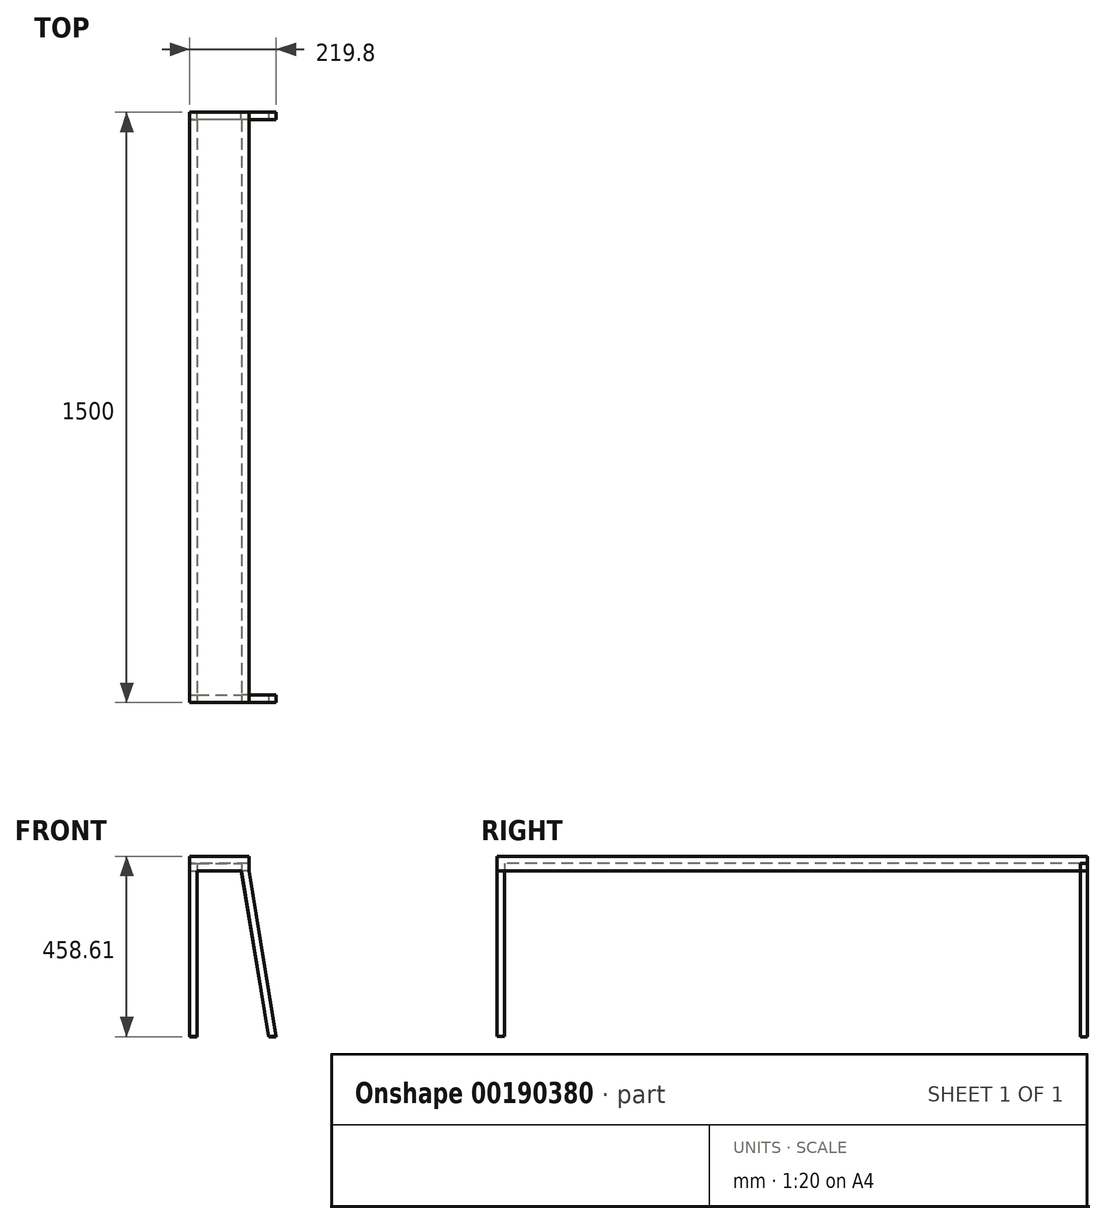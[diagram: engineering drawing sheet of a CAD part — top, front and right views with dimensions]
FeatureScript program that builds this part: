
annotation { "Feature Type Name" : "Feature", "Feature Type Description" : "" }
export const myFeature = defineFeature(function(context is Context, id is Id, definition is map)
    precondition{}
    {
        {
            var Q0;
            Q0=qCreatedBy(makeId("Front.planeOp"),FACE);
            var sketch = newSketch(context, id + "F0", { "sketchPlane" : qUnion([Q0])});
            skLineSegment(sketch, "E0.bottom", {"start": v(-19, 322.25) * mm, "end": v(131, 322.25) * mm});
            skLineSegment(sketch, "E0.top", {"start": v(-19, 303.25) * mm, "end": v(131, 303.25) * mm});
            skLineSegment(sketch, "E0.left", {"start": v(-19, 322.25) * mm, "end": v(-19, 303.25) * mm});
            skLineSegment(sketch, "E0.right", {"start": v(131, 322.25) * mm, "end": v(131, 303.25) * mm});
            skLineSegment(sketch, "E1", {"start": v(-19, 303.25) * mm, "end": v(-19, -116.75) * mm});
            skLineSegment(sketch, "E2", {"start": v(-19, -116.75) * mm, "end": v(0, -116.75) * mm});
            skLineSegment(sketch, "E3", {"start": v(0, -116.75) * mm, "end": v(0, 303.25) * mm});
            skLineSegment(sketch, "E4", {"start": v(131, 303.25) * mm, "end": v(200.52, -116.75) * mm});
            skLineSegment(sketch, "E5", {"start": v(200.52, -116.75) * mm, "end": v(181.52, -116.75) * mm});
            skLineSegment(sketch, "E6", {"start": v(181.52, -116.75) * mm, "end": v(112.45, 303.25) * mm});
            skLineSegment(sketch, "E7.top", {"start": v(-19, 341.25) * mm, "end": v(131, 341.25) * mm});
            skLineSegment(sketch, "E7.left", {"start": v(-19, 322.25) * mm, "end": v(-19, 341.25) * mm});
            skLineSegment(sketch, "E7.right", {"start": v(131, 322.25) * mm, "end": v(131, 341.25) * mm});
            skSolve(sketch);
        }
        {
            var Q0;
            {var subQ0=sQuery(id+"F0.wireOp",EDGE,"E0.left");Q0=makeQuery(id+"F0.imprint","IMPRINT",FACE,{"disambiguationData":[TD([[makeQuery(id+"F0.imprint","IMPRINT",EDGE,{"derivedFrom":subQ0}),1.0]])]});}
            var Q1;
            {var subQ0=sQuery(id+"F0.wireOp",EDGE,"E1");Q1=makeQuery(id+"F0.imprint","IMPRINT",FACE,{"disambiguationData":[TD([[makeQuery(id+"F0.imprint","IMPRINT",EDGE,{"derivedFrom":subQ0}),1.0]])]});}
            var Q2;
            {var subQ0=sQuery(id+"F0.wireOp",EDGE,"E4");Q2=makeQuery(id+"F0.imprint","IMPRINT",FACE,{"disambiguationData":[TD([[makeQuery(id+"F0.imprint","IMPRINT",EDGE,{"derivedFrom":subQ0}),-1.0]])]});}
            extrude(context, id + "F1", {"entities" : qUnion([Q0, Q1, Q2]), "oppositeDirection" : true, "depth" : 19 * mm});
        }
        {
            var Q0;
            Q0=makeQuery(id+"F0.imprint","IMPRINT",FACE,{"disambiguationData":[TD([[makeQuery(id+"F0.imprint","IMPRINT",EDGE,{"derivedFrom":sQuery(id+"F0.wireOp",EDGE,"E0.bottom")}),1.0]])]});
            extrude(context, id + "F2", {"entities" : qUnion([Q0]), "operationType" : NewBodyOperationType.ADD, "oppositeDirection" : true, "depth" : 1500 * mm});
        }
        {
            var Q0;
            Q0=makeQuery(id+"F1.opExtrude","CAP_FACE",FACE,{"disambiguationData":[OSD([sQuery(id+"F0.wireOp",EDGE,"E0.top"),sQuery(id+"F0.wireOp",EDGE,"E0.left"),sQuery(id+"F0.wireOp",EDGE,"E0.right"),sQuery(id+"F0.wireOp",EDGE,"E1"),sQuery(id+"F0.wireOp",EDGE,"E2"),sQuery(id+"F0.wireOp",EDGE,"E3"),sQuery(id+"F0.wireOp",EDGE,"E4"),sQuery(id+"F0.wireOp",EDGE,"E5"),sQuery(id+"F0.wireOp",EDGE,"E6"),sQuery(id+"F0.wireOp",EDGE,"E0.bottom")])],"isStart":false});
            cPlane(context, id + "F3", {"entities" : qUnion([Q0]), "cplaneType" : CPlaneType.OFFSET, "offset" : 0 * mm, "width" : 150 * mm, "height" : 150 * mm});
        }
        {
            var Q0;
            Q0=qCreatedBy(id+"F3.planeOp",FACE);
            var sketch = newSketch(context, id + "F4", { "sketchPlane" : qUnion([Q0])});
            skLineSegment(sketch, "E8.bottom", {"start": v(-131, 322.25) * mm, "end": v(-112, 322.25) * mm});
            skLineSegment(sketch, "E8.top", {"start": v(-131, 303.25) * mm, "end": v(-112, 303.25) * mm});
            skLineSegment(sketch, "E8.left", {"start": v(-131, 322.25) * mm, "end": v(-131, 303.25) * mm});
            skLineSegment(sketch, "E8.right", {"start": v(-112, 322.25) * mm, "end": v(-112, 303.25) * mm});
            skLineSegment(sketch, "E9.bottom", {"start": v(19, 322.25) * mm, "end": v(0, 322.25) * mm});
            skLineSegment(sketch, "E9.top", {"start": v(19, 303.25) * mm, "end": v(0, 303.25) * mm});
            skLineSegment(sketch, "E9.left", {"start": v(19, 322.25) * mm, "end": v(19, 303.25) * mm});
            skLineSegment(sketch, "E9.right", {"start": v(0, 322.25) * mm, "end": v(0, 303.25) * mm});
            skSolve(sketch);
        }
        {
            var Q0;
            Q0 = qSketchRegion(id + "F4", true);
            extrude(context, id + "F5", {"entities" : qUnion([Q0]), "operationType" : NewBodyOperationType.ADD, "depth" : 1462 * mm});
        }
        {
            var Q0;
            Q0=makeQuery(id+"F5.opExtrude","CAP_FACE",FACE,{"disambiguationData":[OSD([sQuery(id+"F4.wireOp",EDGE,"E8.bottom"),sQuery(id+"F4.wireOp",EDGE,"E8.top"),sQuery(id+"F4.wireOp",EDGE,"E8.left"),sQuery(id+"F4.wireOp",EDGE,"E8.right")])],"isStart":false});
            cPlane(context, id + "F6", {"entities" : qUnion([Q0]), "cplaneType" : CPlaneType.OFFSET, "offset" : 19 * mm, "width" : 150 * mm, "height" : 150 * mm});
        }
        {
            var Q0;
            Q0=qCreatedBy(id+"F6.planeOp",FACE);
            var sketch = newSketch(context, id + "F7", { "sketchPlane" : qUnion([Q0])});
            skLineSegment(sketch, "E10.bottom", {"start": v(-131, 322.25) * mm, "end": v(19, 322.25) * mm});
            skLineSegment(sketch, "E10.top", {"start": v(-131, 303.25) * mm, "end": v(19, 303.25) * mm});
            skLineSegment(sketch, "E10.left", {"start": v(-131, 322.25) * mm, "end": v(-131, 303.25) * mm});
            skLineSegment(sketch, "E10.right", {"start": v(19, 322.25) * mm, "end": v(19, 303.25) * mm});
            skLineSegment(sketch, "E11", {"start": v(19, 303.25) * mm, "end": v(19, -117.36) * mm});
            skLineSegment(sketch, "E12", {"start": v(19, -117.36) * mm, "end": v(0, -117.36) * mm});
            skLineSegment(sketch, "E13", {"start": v(0, -117.36) * mm, "end": v(0, 303.25) * mm});
            skLineSegment(sketch, "E14", {"start": v(-131, 303.25) * mm, "end": v(-200.8, -117.36) * mm});
            skLineSegment(sketch, "E15", {"start": v(-200.8, -117.36) * mm, "end": v(-182.02, -117.36) * mm});
            skLineSegment(sketch, "E16", {"start": v(-182.02, -117.36) * mm, "end": v(-111.57, 303.25) * mm});
            skSolve(sketch);
        }
        {
            var Q0;
            Q0 = qSketchRegion(id + "F7", true);
            extrude(context, id + "F8", {"entities" : qUnion([Q0]), "oppositeDirection" : true, "depth" : 19 * mm});
        }
    });
